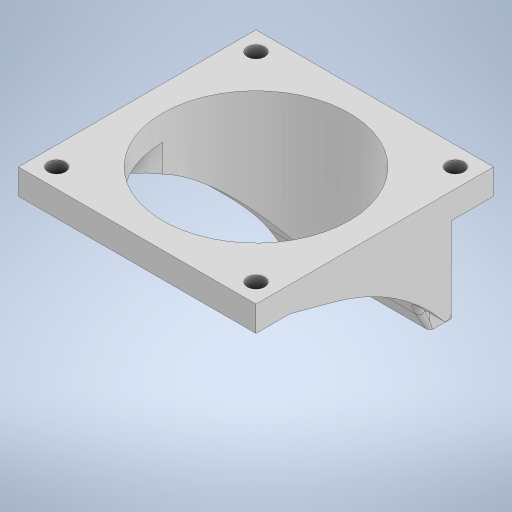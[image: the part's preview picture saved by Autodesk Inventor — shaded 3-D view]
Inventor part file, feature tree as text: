
AUTODESK INVENTOR PART (.ipt)
format: ipt  version: 2024 (Build 280153000, 153)  size: 343,040 bytes
history: native  units: mm
features: extrude x3, fillet x3, sketch x3, projected_geometry x1
ambient origin geometry x8: Origin, YZ Plane, XZ Plane, XY Plane, X Axis, Y Axis, Z Axis, Center Point
bodies: Solid1 (feature_tree)
feature tree (10):
  extrude  "Extrusion1"  Depth=56.0mm
  extrude  "Extrusion2"  Depth=44.0mm
  extrude  "Extrusion3"  Depth=4.1mm
  fillet  "Fillet1"  Radius=4.1mm
  fillet  "Fillet2"  Radius=4.1mm
  fillet  "Fillet3"  Radius=6.0mm
  sketch  "Sketch1"  dims[d0=56.0mm d1=56.0mm]
  sketch  "Sketch2"  dims[d2=4.5mm d3=44.0mm]
  projected_geometry  "Projected Loop1"
  sketch  "Sketch3"  dims[d4=4.1mm d5=4.1mm d6=4.1mm d7=4.1mm d8=6.0mm d9=0.0mm d10=10.0mm d11=10.0mm d12=10.0mm d13=30.0mm d14=0.0mm d15=23.0mm d16=99.0mm d17=0.0mm d18=50.0mm d19=5.0mm d20=1.0mm d21=0.0mm d22=0.0mm]
